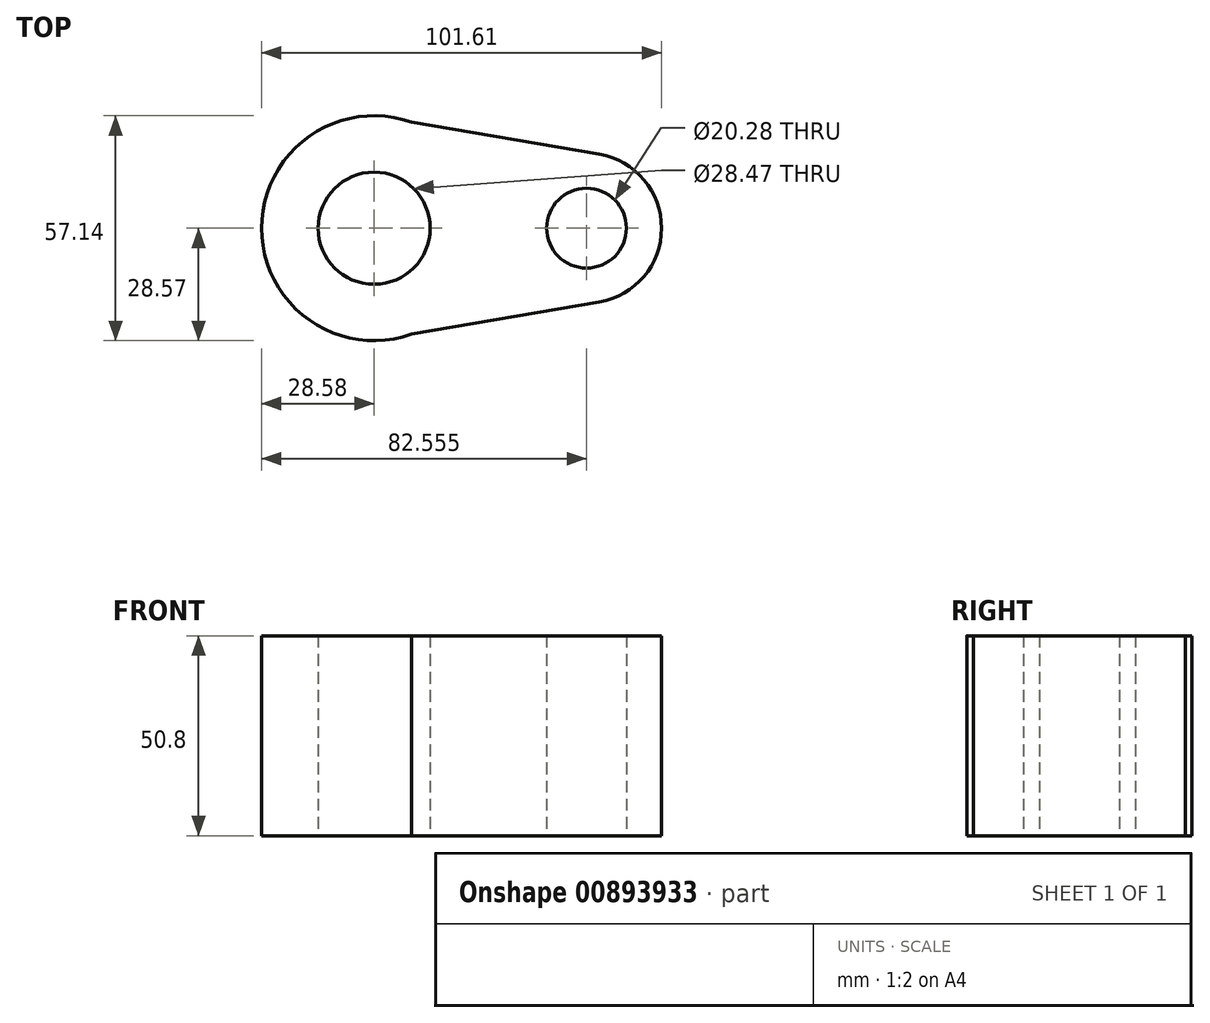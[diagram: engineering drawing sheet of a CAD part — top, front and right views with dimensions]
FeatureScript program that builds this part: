
annotation { "Feature Type Name" : "Feature", "Feature Type Description" : "" }
export const myFeature = defineFeature(function(context is Context, id is Id, definition is map)
    precondition{}
    {
        {
            var Q0;
            Q0=qCreatedBy(makeId("Top.planeOp"),FACE);
            var sketch = newSketch(context, id + "F0", { "sketchPlane" : qUnion([Q0])});
            skArc(sketch, "E0", {"start": v(9.51, 26.95) * mm, "mid": v(-28.58, 0) * mm, "end": v(9.51, -26.95) * mm});
            skArc(sketch, "E1", {"start": v(57.2, -18.78) * mm, "mid": v(73.03, 0) * mm, "end": v(57.2, 18.78) * mm});
            skLineSegment(sketch, "E2", {"start": v(0, 28.58) * mm, "end": v(57.2, 18.78) * mm});
            skLineSegment(sketch, "E3", {"start": v(0, -28.58) * mm, "end": v(57.2, -18.78) * mm});
            skCircle(sketch, "E4", {"center": v(0, 0) * mm, "radius": 14.24 * mm});
            skCircle(sketch, "E5", {"center": v(53.98, 0) * mm, "radius": 10.14 * mm});
            skSolve(sketch);
        }
        {
            var Q0;
            Q0=makeQuery(id+"F0.imprint","IMPRINT",FACE,{"disambiguationData":[TD([[makeQuery(id+"F0.imprint","IMPRINT",EDGE,{"derivedFrom":sQuery(id+"F0.wireOp",EDGE,"E4")}),1.0]])]});
            var Q1;
            Q1=makeQuery(id+"F0.imprint","IMPRINT",FACE,{"disambiguationData":[TD([[makeQuery(id+"F0.imprint","IMPRINT",EDGE,{"derivedFrom":sQuery(id+"F0.wireOp",EDGE,"E5")}),1.0]])]});
            var Q2;
            {var subQ3=sQuery(id+"F0.wireOp",EDGE,"E1");Q2=makeQuery(id+"F0.imprint","IMPRINT",FACE,{"disambiguationData":[TD([[makeQuery(id+"F0.imprint","IMPRINT",EDGE,{"derivedFrom":subQ3}),1.0]])]});}
            var Q3;
            {var subQ0=sQuery(id+"F0.wireOp",EDGE,"E2");var subQ1=sQuery(id+"F0.wireOp",EDGE,"E0");var subQ2=makeQuery(id+"F0.imprint","INTERSECT",VERTEX,{"disambiguationData":[OD(0.0)],"derivedFrom":[subQ1,subQ0]});Q3=makeQuery(id+"F0.imprint","IMPRINT",FACE,{"disambiguationData":[TD([[makeQuery(id+"F0.imprint","IMPRINT",EDGE,{"disambiguationData":[TD([[subQ2,-1.0]])],"derivedFrom":subQ1}),1.0]])]});}
            var Q4;
            {var subQ0=sQuery(id+"F0.wireOp",EDGE,"E3");var subQ1=sQuery(id+"F0.wireOp",EDGE,"E0");var subQ2=makeQuery(id+"F0.imprint","INTERSECT",VERTEX,{"disambiguationData":[OD(0.0)],"derivedFrom":[subQ1,subQ0]});Q4=makeQuery(id+"F0.imprint","IMPRINT",FACE,{"disambiguationData":[TD([[makeQuery(id+"F0.imprint","IMPRINT",EDGE,{"disambiguationData":[TD([[subQ2,1.0]])],"derivedFrom":subQ1}),1.0]])]});}
            var Q5;
            Q5=sQuery(id+"F0.wireOp",EDGE,"E5");
            var Q6;
            Q6=sQuery(id+"F0.wireOp",EDGE,"E4");
            var Q7;
            Q7=sQuery(id+"F0.wireOp",EDGE,"E0");
            var Q8;
            Q8=sQuery(id+"F0.wireOp",EDGE,"E2");
            var Q9;
            Q9=sQuery(id+"F0.wireOp",EDGE,"E1");
            var Q10;
            Q10=sQuery(id+"F0.wireOp",EDGE,"E3");
            extrude(context, id + "F1", {"entities" : qUnion([Q0, Q1, Q2, Q3, Q4]), "surfaceEntities" : qUnion([Q5, Q6, Q7, Q8, Q9, Q10]), "depth" : 50.8 * mm, "offsetDistance" : 25.4 * mm});
        }
        {
            var Q0;
            Q0=makeQuery(id+"F0.imprint","IMPRINT",FACE,{"disambiguationData":[TD([[makeQuery(id+"F0.imprint","IMPRINT",EDGE,{"derivedFrom":sQuery(id+"F0.wireOp",EDGE,"E4")}),1.0]])]});
            var Q1;
            Q1=makeQuery(id+"F0.imprint","IMPRINT",FACE,{"disambiguationData":[TD([[makeQuery(id+"F0.imprint","IMPRINT",EDGE,{"derivedFrom":sQuery(id+"F0.wireOp",EDGE,"E5")}),1.0]])]});
            var Q2;
            Q2=sQuery(id+"F0.wireOp",EDGE,"E4");
            var Q3;
            Q3=sQuery(id+"F0.wireOp",EDGE,"E5");
            extrude(context, id + "F2", {"entities" : qUnion([Q0, Q1]), "operationType" : NewBodyOperationType.REMOVE, "surfaceEntities" : qUnion([Q2, Q3]), "depth" : 114.05 * mm, "offsetDistance" : 25.4 * mm});
        }
    });
